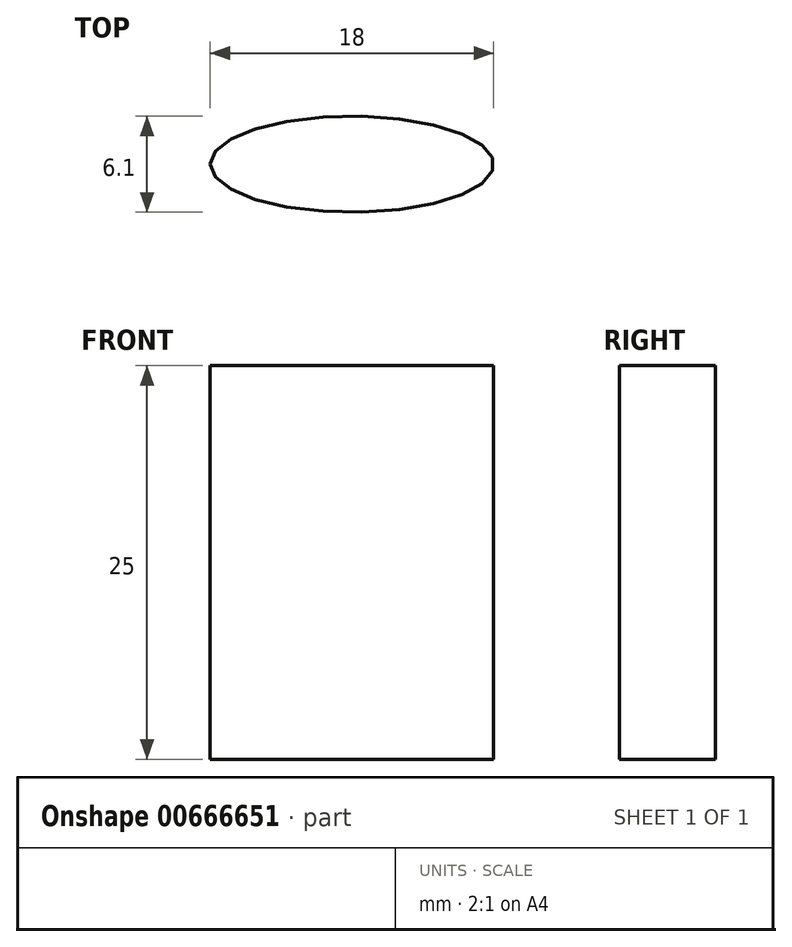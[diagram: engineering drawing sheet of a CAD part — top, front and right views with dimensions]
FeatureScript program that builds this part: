
annotation { "Feature Type Name" : "Feature", "Feature Type Description" : "" }
export const myFeature = defineFeature(function(context is Context, id is Id, definition is map)
    precondition{}
    {
        {
            var Q0;
            Q0=qCreatedBy(makeId("Top.planeOp"),FACE);
            var sketch = newSketch(context, id + "F0", { "sketchPlane" : qUnion([Q0])});
            skEllipse(sketch, "E0", {"center": v(0, 0) * mm, "majorRadius": 9 * mm, "minorRadius": 3.05 * mm, "majorAxis": v(-1, 0)});
            skSolve(sketch);
        }
        {
            var Q0;
            Q0 = qSketchRegion(id + "F0", true);
            extrude(context, id + "F1", {"entities" : qUnion([Q0]), "depth" : 25 * mm, "offsetDistance" : 25 * mm});
        }
    });
